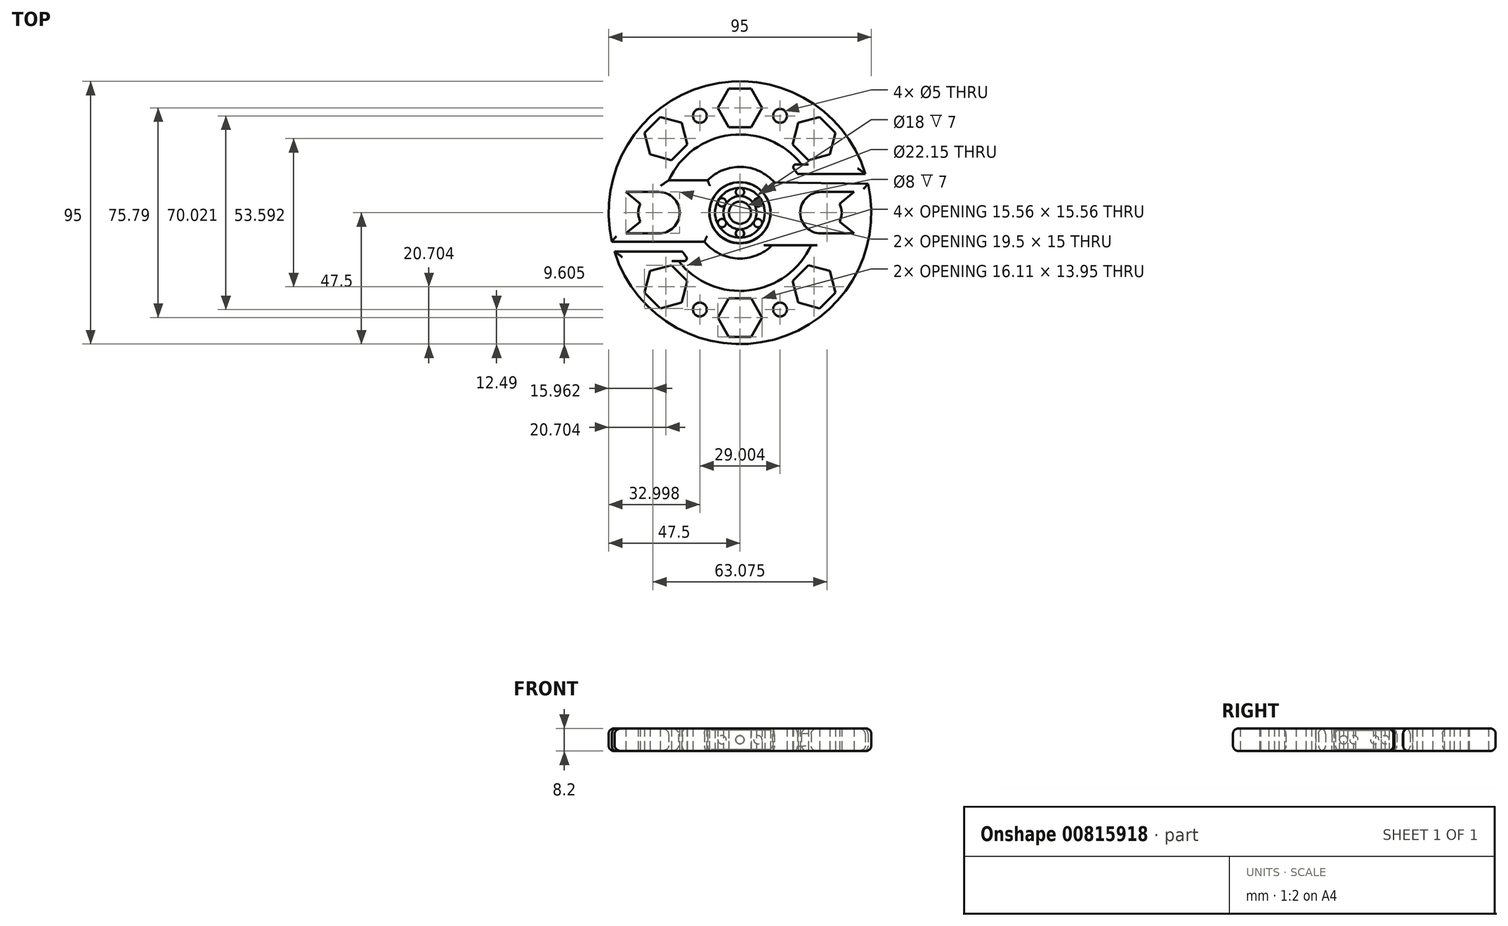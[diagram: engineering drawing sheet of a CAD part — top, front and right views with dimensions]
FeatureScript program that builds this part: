
annotation { "Feature Type Name" : "Feature", "Feature Type Description" : "" }
export const myFeature = defineFeature(function(context is Context, id is Id, definition is map)
    precondition{}
    {
        {
            var Q0;
            Q0=qCreatedBy(makeId("Top.planeOp"),FACE);
            var sketch = newSketch(context, id + "F0", { "sketchPlane" : qUnion([Q0])});
            skArc(sketch, "E0", {"start": v(45.38, 14.04) * mm, "mid": v(-10.46, 46.33) * mm, "end": v(-47, -6.81) * mm});
            skLineSegment(sketch, "E1.top", {"start": v(-45.38, -14.04) * mm, "end": v(-24.56, -14.04) * mm});
            skCircle(sketch, "E2", {"center": v(0, 0) * mm, "radius": 11.07 * mm});
            skArc(sketch, "E3", {"start": v(22.24, 17.5) * mm, "mid": v(-3.38, 28.09) * mm, "end": v(-25.75, 11.72) * mm});
            skArc(sketch, "E4.trimOffspring", {"start": v(-22.2, -17.54) * mm, "mid": v(3.4, -28.08) * mm, "end": v(25.75, -11.72) * mm});
            skArc(sketch, "E5.trimOffspring", {"start": v(-45.38, -14.04) * mm, "mid": v(10.5, -46.32) * mm, "end": v(47, 6.9) * mm});
            skLineSegment(sketch, "E6.trimOffspring", {"start": v(24.59, 14) * mm, "end": v(45.38, 14.04) * mm});
            skPoint(sketch, "E7.trimOffspring.end.orphan", {"position": v(45.38, -14.04) * mm});
            skPoint(sketch, "E1.bottom.start.orphan", {"position": v(-45.38, 14.04) * mm});
            skPoint(sketch, "E8.orphan", {"position": v(47, -6.9) * mm});
            skPoint(sketch, "E9.orphan", {"position": v(-47, 6.81) * mm});
            skArc(sketch, "E10", {"start": v(-12.86, -10.46) * mm, "mid": v(-0.85, -16.55) * mm, "end": v(11.72, -11.72) * mm});
            skArc(sketch, "E11.trimOffspring", {"start": v(12.47, 10.92) * mm, "mid": v(0.55, 16.57) * mm, "end": v(-11.72, 11.72) * mm});
            skLineSegment(sketch, "E12.trimOffspring", {"start": v(-8.7, 6.85) * mm, "end": v(8.59, 7) * mm});
            skLineSegment(sketch, "E13.trimOffspring", {"start": v(-8.7, -6.85) * mm, "end": v(8.69, -6.87) * mm});
            skLineSegment(sketch, "E14", {"start": v(-7.83, 7.83) * mm, "end": v(-6.87, 6.87) * mm});
            skLineSegment(sketch, "E15", {"start": v(6.87, -6.87) * mm, "end": v(7.83, -7.83) * mm});
            skLineSegment(sketch, "E16", {"start": v(-11.72, 11.72) * mm, "end": v(-25.75, 11.72) * mm});
            skLineSegment(sketch, "E17", {"start": v(11.72, -11.72) * mm, "end": v(11.72, -11.72) * mm});
            skArc(sketch, "E18", {"start": v(20.88, 14) * mm, "mid": v(19.54, 15.8) * mm, "end": v(18.05, 17.5) * mm});
            skLineSegment(sketch, "E19", {"start": v(-24.56, -14.04) * mm, "end": v(-20.85, -14.04) * mm});
            skLineSegment(sketch, "E20", {"start": v(24.59, 14) * mm, "end": v(20.88, 14) * mm});
            skLineSegment(sketch, "E21", {"start": v(22.24, 17.5) * mm, "end": v(18.05, 17.5) * mm});
            skLineSegment(sketch, "E22", {"start": v(-22.2, -17.54) * mm, "end": v(-18, -17.54) * mm});
            skArc(sketch, "E23.trimOffspring", {"start": v(-20.85, -14.04) * mm, "mid": v(-19.5, -15.85) * mm, "end": v(-18, -17.54) * mm});
            skLineSegment(sketch, "E24", {"start": v(0, 0) * mm, "end": v(0, 16.57) * mm, "construction": true});
            skLineSegment(sketch, "E25", {"start": v(-6.87, 6.87) * mm, "end": v(-11.72, 11.72) * mm, "construction": true});
            skLineSegment(sketch, "E26", {"start": v(0, 0) * mm, "end": v(11.72, 11.72) * mm, "construction": true});
            skLineSegment(sketch, "E27", {"start": v(6.87, -6.87) * mm, "end": v(11.72, -11.72) * mm, "construction": true});
            skLineSegment(sketch, "E28", {"start": v(0, 0) * mm, "end": v(0, -16.57) * mm, "construction": true});
            skLineSegment(sketch, "E29", {"start": v(0, 0) * mm, "end": v(-11.72, -11.72) * mm, "construction": true});
            skLineSegment(sketch, "E30.trimOffspring", {"start": v(-20, 20) * mm, "end": v(-33.59, 33.59) * mm, "construction": true});
            skLineSegment(sketch, "E31.trimOffspring", {"start": v(0, 28.29) * mm, "end": v(0, 47.5) * mm, "construction": true});
            skLineSegment(sketch, "E32.trimOffspring", {"start": v(20, 20) * mm, "end": v(33.59, 33.59) * mm, "construction": true});
            skLineSegment(sketch, "E33.trimOffspring", {"start": v(20, -20) * mm, "end": v(33.59, -33.59) * mm, "construction": true});
            skLineSegment(sketch, "E34.trimOffspring", {"start": v(0, -28.29) * mm, "end": v(0, -47.5) * mm, "construction": true});
            skLineSegment(sketch, "E35.trimOffspring", {"start": v(-20, -20) * mm, "end": v(-33.59, -33.59) * mm, "construction": true});
            skPoint(sketch, "E36", {"position": v(0, 37.9) * mm});
            skPoint(sketch, "E37", {"position": v(-26.8, 26.8) * mm});
            skPoint(sketch, "E38", {"position": v(26.8, 26.8) * mm});
            skPoint(sketch, "E39", {"position": v(26.8, -26.8) * mm});
            skPoint(sketch, "E40", {"position": v(0, -37.9) * mm});
            skPoint(sketch, "E41", {"position": v(-26.8, -26.8) * mm});
            skLineSegment(sketch, "E42.0", {"start": v(-32.5, 21.1) * mm, "end": v(-34.58, 28.88) * mm});
            skLineSegment(sketch, "E42.1", {"start": v(-34.58, 28.88) * mm, "end": v(-28.88, 34.58) * mm});
            skLineSegment(sketch, "E42.2", {"start": v(-28.88, 34.58) * mm, "end": v(-21.1, 32.5) * mm});
            skLineSegment(sketch, "E42.3", {"start": v(-21.1, 32.5) * mm, "end": v(-19.02, 24.71) * mm});
            skLineSegment(sketch, "E42.4", {"start": v(-19.02, 24.71) * mm, "end": v(-24.71, 19.02) * mm});
            skLineSegment(sketch, "E42.5", {"start": v(-24.71, 19.02) * mm, "end": v(-32.5, 21.1) * mm});
            skLineSegment(sketch, "E43.0", {"start": v(21.1, -32.5) * mm, "end": v(19.02, -24.71) * mm});
            skLineSegment(sketch, "E43.1", {"start": v(19.02, -24.71) * mm, "end": v(24.71, -19.02) * mm});
            skLineSegment(sketch, "E43.2", {"start": v(24.71, -19.02) * mm, "end": v(32.5, -21.1) * mm});
            skLineSegment(sketch, "E43.3", {"start": v(32.5, -21.1) * mm, "end": v(34.58, -28.88) * mm});
            skLineSegment(sketch, "E43.4", {"start": v(34.58, -28.88) * mm, "end": v(28.88, -34.58) * mm});
            skLineSegment(sketch, "E43.5", {"start": v(28.88, -34.58) * mm, "end": v(21.1, -32.5) * mm});
            skLineSegment(sketch, "E44.0", {"start": v(-8.05, 37.9) * mm, "end": v(-4.03, 44.87) * mm});
            skLineSegment(sketch, "E44.1", {"start": v(-4.03, 44.87) * mm, "end": v(4.03, 44.87) * mm});
            skLineSegment(sketch, "E44.2", {"start": v(4.03, 44.87) * mm, "end": v(8.05, 37.9) * mm});
            skLineSegment(sketch, "E44.3", {"start": v(8.05, 37.9) * mm, "end": v(4.03, 30.92) * mm});
            skLineSegment(sketch, "E44.4", {"start": v(4.03, 30.92) * mm, "end": v(-4.03, 30.92) * mm});
            skLineSegment(sketch, "E44.5", {"start": v(-4.03, 30.92) * mm, "end": v(-8.05, 37.9) * mm});
            skLineSegment(sketch, "E45.0", {"start": v(-8.05, -37.9) * mm, "end": v(-4.03, -30.92) * mm});
            skLineSegment(sketch, "E45.1", {"start": v(-4.03, -30.92) * mm, "end": v(4.03, -30.92) * mm});
            skLineSegment(sketch, "E45.2", {"start": v(4.03, -30.92) * mm, "end": v(8.05, -37.9) * mm});
            skLineSegment(sketch, "E45.3", {"start": v(8.05, -37.9) * mm, "end": v(4.03, -44.87) * mm});
            skLineSegment(sketch, "E45.4", {"start": v(4.03, -44.87) * mm, "end": v(-4.03, -44.87) * mm});
            skLineSegment(sketch, "E45.5", {"start": v(-4.03, -44.87) * mm, "end": v(-8.05, -37.9) * mm});
            skLineSegment(sketch, "E46.0", {"start": v(-32.5, -21.1) * mm, "end": v(-24.71, -19.02) * mm});
            skLineSegment(sketch, "E46.1", {"start": v(-24.71, -19.02) * mm, "end": v(-19.02, -24.71) * mm});
            skLineSegment(sketch, "E46.2", {"start": v(-19.02, -24.71) * mm, "end": v(-21.1, -32.5) * mm});
            skLineSegment(sketch, "E46.3", {"start": v(-21.1, -32.5) * mm, "end": v(-28.88, -34.58) * mm});
            skLineSegment(sketch, "E46.4", {"start": v(-28.88, -34.58) * mm, "end": v(-34.58, -28.88) * mm});
            skLineSegment(sketch, "E46.5", {"start": v(-34.58, -28.88) * mm, "end": v(-32.5, -21.1) * mm});
            skLineSegment(sketch, "E47.0", {"start": v(21.1, 32.5) * mm, "end": v(28.88, 34.58) * mm});
            skLineSegment(sketch, "E47.1", {"start": v(28.88, 34.58) * mm, "end": v(34.58, 28.88) * mm});
            skLineSegment(sketch, "E47.2", {"start": v(34.58, 28.88) * mm, "end": v(32.5, 21.1) * mm});
            skLineSegment(sketch, "E47.3", {"start": v(32.5, 21.1) * mm, "end": v(24.71, 19.02) * mm});
            skLineSegment(sketch, "E47.4", {"start": v(24.71, 19.02) * mm, "end": v(19.02, 24.71) * mm});
            skLineSegment(sketch, "E47.5", {"start": v(19.02, 24.71) * mm, "end": v(21.1, 32.5) * mm});
            skArc(sketch, "E48", {"start": v(-45.38, -14.04) * mm, "mid": v(10.5, -46.32) * mm, "end": v(47, 6.9) * mm, "construction": true});
            skArc(sketch, "E49", {"start": v(-47, -6.81) * mm, "mid": v(-46.7, -8.64) * mm, "end": v(-46.33, -10.46) * mm});
            skPoint(sketch, "E50", {"position": v(-46.33, -10.46) * mm});
            skArc(sketch, "E51", {"start": v(45.38, 14.04) * mm, "mid": v(-10.46, 46.33) * mm, "end": v(-47, -6.81) * mm, "construction": true});
            skArc(sketch, "E52", {"start": v(47, 6.9) * mm, "mid": v(46.7, 8.71) * mm, "end": v(46.32, 10.5) * mm});
            skPoint(sketch, "E53", {"position": v(46.32, 10.5) * mm});
            skLineSegment(sketch, "E54", {"start": v(-46.33, -10.46) * mm, "end": v(-36.42, -10.46) * mm});
            skLineSegment(sketch, "E55", {"start": v(46.32, 10.5) * mm, "end": v(12.47, 10.92) * mm});
            skPoint(sketch, "E56", {"position": v(-114.88, 3.23) * mm});
            skLineSegment(sketch, "E57.0", {"start": v(-114.88, 9.7) * mm, "end": v(-109.28, 6.47) * mm});
            skLineSegment(sketch, "E57.1", {"start": v(-109.28, 6.47) * mm, "end": v(-109.28, 0) * mm});
            skLineSegment(sketch, "E57.2", {"start": v(-109.28, 0) * mm, "end": v(-114.88, -3.23) * mm});
            skLineSegment(sketch, "E57.3", {"start": v(-114.88, -3.23) * mm, "end": v(-120.48, 0) * mm});
            skLineSegment(sketch, "E57.4", {"start": v(-120.48, 0) * mm, "end": v(-120.48, 6.47) * mm});
            skLineSegment(sketch, "E57.5", {"start": v(-120.48, 6.47) * mm, "end": v(-114.88, 9.7) * mm});
            skPoint(sketch, "E58", {"position": v(-130.27, -23) * mm});
            skLineSegment(sketch, "E59.0", {"start": v(-130.27, -16.53) * mm, "end": v(-124.67, -19.77) * mm});
            skLineSegment(sketch, "E59.1", {"start": v(-124.67, -19.77) * mm, "end": v(-124.67, -26.23) * mm});
            skLineSegment(sketch, "E59.2", {"start": v(-124.67, -26.23) * mm, "end": v(-130.27, -29.47) * mm});
            skLineSegment(sketch, "E59.3", {"start": v(-130.27, -29.47) * mm, "end": v(-135.87, -26.23) * mm});
            skLineSegment(sketch, "E59.4", {"start": v(-135.87, -26.23) * mm, "end": v(-135.87, -19.77) * mm});
            skLineSegment(sketch, "E59.5", {"start": v(-135.87, -19.77) * mm, "end": v(-130.27, -16.53) * mm});
            skLineSegment(sketch, "E60", {"start": v(-11.07, 0) * mm, "end": v(-47.5, 0) * mm, "construction": true});
            skLineSegment(sketch, "E61", {"start": v(11.07, 0) * mm, "end": v(47.5, 0) * mm, "construction": true});
            skLineSegment(sketch, "E62.0", {"start": v(-137.37, -18.9) * mm, "end": v(-130.27, -14.8) * mm});
            skLineSegment(sketch, "E62.1", {"start": v(-123.17, -18.9) * mm, "end": v(-123.17, -27.1) * mm});
            skLineSegment(sketch, "E62.2", {"start": v(-123.17, -27.1) * mm, "end": v(-130.27, -31.2) * mm});
            skLineSegment(sketch, "E62.3", {"start": v(-130.27, -14.8) * mm, "end": v(-123.17, -18.9) * mm});
            skLineSegment(sketch, "E62.4", {"start": v(-130.27, -31.2) * mm, "end": v(-137.37, -27.1) * mm});
            skLineSegment(sketch, "E62.5", {"start": v(-137.37, -27.1) * mm, "end": v(-137.37, -18.9) * mm});
            skLineSegment(sketch, "E63.0", {"start": v(-138.87, -18.03) * mm, "end": v(-130.27, -13.07) * mm});
            skLineSegment(sketch, "E63.1", {"start": v(-121.67, -18.03) * mm, "end": v(-121.67, -27.97) * mm});
            skLineSegment(sketch, "E63.2", {"start": v(-121.67, -27.97) * mm, "end": v(-130.27, -32.93) * mm});
            skLineSegment(sketch, "E63.3", {"start": v(-130.27, -13.07) * mm, "end": v(-121.67, -18.03) * mm});
            skLineSegment(sketch, "E63.4", {"start": v(-130.27, -32.93) * mm, "end": v(-138.87, -27.97) * mm});
            skLineSegment(sketch, "E63.5", {"start": v(-138.87, -27.97) * mm, "end": v(-138.87, -18.03) * mm});
            skPoint(sketch, "E64", {"position": v(-99.9, -24.26) * mm});
            skLineSegment(sketch, "E65.0", {"start": v(-109.83, -24.26) * mm, "end": v(-104.87, -15.66) * mm});
            skLineSegment(sketch, "E65.1", {"start": v(-94.94, -15.66) * mm, "end": v(-89.97, -24.26) * mm});
            skLineSegment(sketch, "E65.2", {"start": v(-89.97, -24.26) * mm, "end": v(-94.94, -32.86) * mm});
            skLineSegment(sketch, "E65.3", {"start": v(-104.87, -15.66) * mm, "end": v(-94.94, -15.66) * mm});
            skLineSegment(sketch, "E65.4", {"start": v(-94.94, -32.86) * mm, "end": v(-104.87, -32.86) * mm});
            skLineSegment(sketch, "E65.5", {"start": v(-104.87, -32.86) * mm, "end": v(-109.83, -24.26) * mm});
            skLineSegment(sketch, "E66.0", {"start": v(-107.82, -22.14) * mm, "end": v(-102.03, -16.34) * mm});
            skLineSegment(sketch, "E66.1", {"start": v(-94.1, -18.47) * mm, "end": v(-91.98, -26.38) * mm});
            skLineSegment(sketch, "E66.2", {"start": v(-91.98, -26.38) * mm, "end": v(-97.78, -32.18) * mm});
            skLineSegment(sketch, "E66.3", {"start": v(-102.03, -16.34) * mm, "end": v(-94.1, -18.47) * mm});
            skLineSegment(sketch, "E66.4", {"start": v(-97.78, -32.18) * mm, "end": v(-105.7, -30.06) * mm});
            skLineSegment(sketch, "E66.5", {"start": v(-105.7, -30.06) * mm, "end": v(-107.82, -22.14) * mm});
            skLineSegment(sketch, "E67.0", {"start": v(-99.9, -17.8) * mm, "end": v(-94.3, -21.03) * mm});
            skLineSegment(sketch, "E67.1", {"start": v(-94.3, -21.03) * mm, "end": v(-94.3, -27.5) * mm});
            skLineSegment(sketch, "E67.2", {"start": v(-94.3, -27.5) * mm, "end": v(-99.9, -30.73) * mm});
            skLineSegment(sketch, "E67.3", {"start": v(-99.9, -30.73) * mm, "end": v(-105.5, -27.5) * mm});
            skLineSegment(sketch, "E67.4", {"start": v(-105.5, -27.5) * mm, "end": v(-105.5, -21.03) * mm});
            skLineSegment(sketch, "E67.5", {"start": v(-105.5, -21.03) * mm, "end": v(-99.9, -17.8) * mm});
            skLineSegment(sketch, "E68.0", {"start": v(-111.57, -24.26) * mm, "end": v(-105.73, -14.16) * mm});
            skLineSegment(sketch, "E68.1", {"start": v(-94.07, -14.16) * mm, "end": v(-88.24, -24.26) * mm});
            skLineSegment(sketch, "E68.2", {"start": v(-88.24, -24.26) * mm, "end": v(-94.07, -34.36) * mm});
            skLineSegment(sketch, "E68.3", {"start": v(-105.73, -14.16) * mm, "end": v(-94.07, -14.16) * mm});
            skLineSegment(sketch, "E68.4", {"start": v(-94.07, -34.36) * mm, "end": v(-105.73, -34.36) * mm});
            skLineSegment(sketch, "E68.5", {"start": v(-105.73, -34.36) * mm, "end": v(-111.57, -24.26) * mm});
            skArc(sketch, "E69", {"start": v(-12.86, -10.46) * mm, "mid": v(16.55, -0.85) * mm, "end": v(-11.72, 11.72) * mm, "construction": true});
            skArc(sketch, "E70", {"start": v(-11.72, 11.72) * mm, "mid": v(-16.55, 0.85) * mm, "end": v(-12.86, -10.46) * mm, "construction": true});
            skLineSegment(sketch, "E71", {"start": v(11.72, -11.72) * mm, "end": v(25.75, -11.72) * mm});
            skLineSegment(sketch, "E72", {"start": v(12.47, 10.92) * mm, "end": v(12.47, 10.92) * mm});
            skArc(sketch, "E73", {"start": v(-20.87, 31.63) * mm, "mid": v(-26.8, 26.8) * mm, "end": v(-31.63, 20.87) * mm, "construction": true});
            skArc(sketch, "E74", {"start": v(-7.6, 37.12) * mm, "mid": v(-14.5, 35.01) * mm, "end": v(-20.87, 31.63) * mm, "construction": true});
            skArc(sketch, "E75", {"start": v(7.6, 37.12) * mm, "mid": v(0, 37.9) * mm, "end": v(-7.6, 37.12) * mm, "construction": true});
            skArc(sketch, "E76", {"start": v(20.87, 31.63) * mm, "mid": v(14.5, 35.01) * mm, "end": v(7.6, 37.12) * mm, "construction": true});
            skCircle(sketch, "E77", {"center": v(-14.5, 35.01) * mm, "radius": 2.5 * mm});
            skCircle(sketch, "E78", {"center": v(14.5, 35.01) * mm, "radius": 2.5 * mm});
            skCircle(sketch, "E79.MirrorC", {"center": v(-14.5, -35.01) * mm, "radius": 2.5 * mm});
            skCircle(sketch, "E80.MirrorC", {"center": v(14.5, -35.01) * mm, "radius": 2.5 * mm});
            skLineSegment(sketch, "E81", {"start": v(-31.63, 20.87) * mm, "end": v(-31.63, 20.87) * mm});
            skLineSegment(sketch, "E82", {"start": v(-36.42, -10.46) * mm, "end": v(-12.86, -10.46) * mm});
            skPoint(sketch, "E83", {"position": v(-31.63, 20.87) * mm});
            skPoint(sketch, "E84", {"position": v(-36.42, -10.46) * mm});
            skArc(sketch, "E85", {"start": v(-31.63, 20.87) * mm, "mid": v(-37.46, 5.73) * mm, "end": v(-36.42, -10.46) * mm, "construction": true});
            skArc(sketch, "E86", {"start": v(-36.42, -10.46) * mm, "mid": v(22.43, -30.54) * mm, "end": v(20.87, 31.63) * mm, "construction": true});
            skPoint(sketch, "E87", {"position": v(-37.04, -8) * mm});
            skCircle(sketch, "E88", {"center": v(-72.26, 0) * mm, "radius": 7.5 * mm});
            skLineSegment(sketch, "E89", {"start": v(-72.26, 7.5) * mm, "end": v(-84.26, 7.5) * mm});
            skLineSegment(sketch, "E90", {"start": v(-84.26, 7.5) * mm, "end": v(-79.03, 3.23) * mm});
            skLineSegment(sketch, "E91.MirrorCS", {"start": v(-72.26, 11.35) * mm, "end": v(-72.26, 11.35) * mm});
            skLineSegment(sketch, "E92.MirrorCS", {"start": v(-84.26, -7.5) * mm, "end": v(-79.03, -3.23) * mm});
            skPoint(sketch, "E93", {"position": v(-72.26, 11.35) * mm});
            skLineSegment(sketch, "E94", {"start": v(-84.26, -7.5) * mm, "end": v(-72.26, -7.5) * mm});
            skCircle(sketch, "E95", {"center": v(-29.29, 0) * mm, "radius": 7.5 * mm});
            skLineSegment(sketch, "E96", {"start": v(-29.29, 7.5) * mm, "end": v(-41.29, 7.5) * mm});
            skLineSegment(sketch, "E97", {"start": v(-41.29, 7.5) * mm, "end": v(-36.06, 3.23) * mm});
            skLineSegment(sketch, "E98.MirrorCS", {"start": v(-58.17, -2.6) * mm, "end": v(-58.17, -2.6) * mm});
            skLineSegment(sketch, "E99.MirrorCS", {"start": v(-41.29, -7.5) * mm, "end": v(-36.06, -3.23) * mm});
            skPoint(sketch, "E100", {"position": v(-29.29, 11.35) * mm});
            skLineSegment(sketch, "E101", {"start": v(-41.29, -7.5) * mm, "end": v(-29.29, -7.5) * mm});
            skCircle(sketch, "E102", {"center": v(29.29, 0) * mm, "radius": 7.5 * mm});
            skLineSegment(sketch, "E103", {"start": v(29.29, -7.5) * mm, "end": v(41.29, -7.5) * mm});
            skLineSegment(sketch, "E104", {"start": v(41.29, -7.5) * mm, "end": v(36.06, -3.23) * mm});
            skLineSegment(sketch, "E105.MirrorCS", {"start": v(-45.35, -43.19) * mm, "end": v(-45.35, -43.19) * mm});
            skLineSegment(sketch, "E106.MirrorCS", {"start": v(41.29, 7.5) * mm, "end": v(36.06, 3.23) * mm});
            skPoint(sketch, "E107", {"position": v(29.29, -11.35) * mm});
            skLineSegment(sketch, "E108", {"start": v(41.29, 7.5) * mm, "end": v(29.29, 7.5) * mm});
            skSolve(sketch);
        }
        {
            var Q0;
            Q0=makeQuery(id+"F0.imprint","IMPRINT",FACE,{"disambiguationData":[TD([[makeQuery(id+"F0.imprint","IMPRINT",EDGE,{"derivedFrom":sQuery(id+"F0.wireOp",EDGE,"E0")}),1.0]])]});
            extrude(context, id + "F1", {"entities" : qUnion([Q0]), "endBound" : BoundingType.SYMMETRIC, "depth" : 8.2 * mm, "offsetDistance" : 25 * mm});
        }
        {
            var Q0;
            Q0=makeQuery(id+"F1.opExtrude","CAP_EDGE",EDGE,{"disambiguationData":[OSD([sQuery(id+"F0.wireOp",EDGE,"E0")])],"isStart":false});
            var Q1;
            Q1=makeQuery(id+"F1.opExtrude","CAP_EDGE",EDGE,{"disambiguationData":[OSD([sQuery(id+"F0.wireOp",EDGE,"E5.trimOffspring")])],"isStart":false});
            var Q2;
            Q2=makeQuery(id+"F1.opExtrude","CAP_EDGE",EDGE,{"disambiguationData":[OSD([sQuery(id+"F0.wireOp",EDGE,"E0")])],"isStart":true});
            var Q3;
            Q3=makeQuery(id+"F1.opExtrude","CAP_EDGE",EDGE,{"disambiguationData":[OSD([sQuery(id+"F0.wireOp",EDGE,"E5.trimOffspring")])],"isStart":true});
            var Q4;
            Q4=makeQuery(id+"F1.opExtrude","CAP_EDGE",EDGE,{"disambiguationData":[OSD([sQuery(id+"F0.wireOp",EDGE,"E1.top"),sQuery(id+"F0.wireOp",EDGE,"E19")])],"isStart":true});
            var Q5;
            Q5=makeQuery(id+"F1.opExtrude","CAP_EDGE",EDGE,{"disambiguationData":[OSD([sQuery(id+"F0.wireOp",EDGE,"E1.top"),sQuery(id+"F0.wireOp",EDGE,"E19")])],"isStart":false});
            var Q6;
            Q6=makeQuery(id+"F1.opExtrude","CAP_EDGE",EDGE,{"disambiguationData":[OSD([sQuery(id+"F0.wireOp",EDGE,"af73f036-c247-4c71-b03d-1512b0a657ec.trimOffspring")])],"isStart":true});
            var Q7;
            Q7=makeQuery(id+"F1.opExtrude","CAP_EDGE",EDGE,{"disambiguationData":[OSD([sQuery(id+"F0.wireOp",EDGE,"af73f036-c247-4c71-b03d-1512b0a657ec.trimOffspring")])],"isStart":false});
            var Q8;
            Q8=makeQuery(id+"F1.opExtrude","CAP_EDGE",EDGE,{"disambiguationData":[OSD([sQuery(id+"F0.wireOp",EDGE,"E11.trimOffspring")])],"isStart":false});
            var Q9;
            Q9=makeQuery(id+"F1.opExtrude","CAP_EDGE",EDGE,{"disambiguationData":[OSD([sQuery(id+"F0.wireOp",EDGE,"E11.trimOffspring")])],"isStart":true});
            var Q10;
            Q10=makeQuery(id+"F1.opExtrude","CAP_EDGE",EDGE,{"disambiguationData":[OSD([sQuery(id+"F0.wireOp",EDGE,"E16")])],"isStart":false});
            var Q11;
            Q11=makeQuery(id+"F1.opExtrude","CAP_EDGE",EDGE,{"disambiguationData":[OSD([sQuery(id+"F0.wireOp",EDGE,"E16")])],"isStart":true});
            var Q12;
            Q12=makeQuery(id+"F1.opExtrude","CAP_EDGE",EDGE,{"disambiguationData":[OSD([sQuery(id+"F0.wireOp",EDGE,"E4.trimOffspring")])],"isStart":true});
            var Q13;
            Q13=makeQuery(id+"F1.opExtrude","CAP_EDGE",EDGE,{"disambiguationData":[OSD([sQuery(id+"F0.wireOp",EDGE,"E4.trimOffspring")])],"isStart":false});
            var Q14;
            Q14=makeQuery(id+"F1.opExtrude","CAP_EDGE",EDGE,{"disambiguationData":[OSD([sQuery(id+"F0.wireOp",EDGE,"E3")])],"isStart":false});
            var Q15;
            Q15=makeQuery(id+"F1.opExtrude","CAP_EDGE",EDGE,{"disambiguationData":[OSD([sQuery(id+"F0.wireOp",EDGE,"E3")])],"isStart":true});
            var Q16;
            Q16=makeQuery(id+"F1.opExtrude","CAP_EDGE",EDGE,{"disambiguationData":[OSD([sQuery(id+"F0.wireOp",EDGE,"E17")])],"isStart":false});
            var Q17;
            Q17=makeQuery(id+"F1.opExtrude","CAP_EDGE",EDGE,{"disambiguationData":[OSD([sQuery(id+"F0.wireOp",EDGE,"E17")])],"isStart":true});
            var Q18;
            Q18=makeQuery(id+"F1.opExtrude","CAP_EDGE",EDGE,{"disambiguationData":[OSD([sQuery(id+"F0.wireOp",EDGE,"E10")])],"isStart":false});
            var Q19;
            Q19=makeQuery(id+"F1.opExtrude","CAP_EDGE",EDGE,{"disambiguationData":[OSD([sQuery(id+"F0.wireOp",EDGE,"E10")])],"isStart":true});
            var Q20;
            Q20=makeQuery(id+"F1.opExtrude","CAP_EDGE",EDGE,{"disambiguationData":[OSD([sQuery(id+"F0.wireOp",EDGE,"318f1a37-417c-41ab-8845-f020125537680.MirrorCS")])],"isStart":false});
            var Q21;
            Q21=makeQuery(id+"F1.opExtrude","CAP_EDGE",EDGE,{"disambiguationData":[OSD([sQuery(id+"F0.wireOp",EDGE,"318f1a37-417c-41ab-8845-f020125537680.MirrorCS")])],"isStart":true});
            var Q22;
            Q22=makeQuery(id+"F1.opExtrude","CAP_EDGE",EDGE,{"disambiguationData":[OSD([sQuery(id+"F0.wireOp",EDGE,"E6.trimOffspring")])],"isStart":false});
            var Q23;
            Q23=makeQuery(id+"F1.opExtrude","CAP_EDGE",EDGE,{"disambiguationData":[OSD([sQuery(id+"F0.wireOp",EDGE,"E6.trimOffspring")])],"isStart":true});
            var Q24;
            Q24=makeQuery(id+"F1.opExtrude","CAP_EDGE",EDGE,{"disambiguationData":[OSD([sQuery(id+"F0.wireOp",EDGE,"E54")])],"isStart":false});
            var Q25;
            Q25=makeQuery(id+"F1.opExtrude","CAP_EDGE",EDGE,{"disambiguationData":[OSD([sQuery(id+"F0.wireOp",EDGE,"E54")])],"isStart":true});
            var Q26;
            Q26=makeQuery(id+"F1.opExtrude","CAP_EDGE",EDGE,{"disambiguationData":[OSD([sQuery(id+"F0.wireOp",EDGE,"E55")])],"isStart":true});
            var Q27;
            Q27=makeQuery(id+"F1.opExtrude","CAP_EDGE",EDGE,{"disambiguationData":[OSD([sQuery(id+"F0.wireOp",EDGE,"E55")])],"isStart":false});
            fillet(context, id + "F2", {"entities" : qUnion([Q0, Q1, Q2, Q3, Q4, Q5, Q6, Q7, Q8, Q9, Q10, Q11, Q12, Q13, Q14, Q15, Q16, Q17, Q18, Q19, Q20, Q21, Q22, Q23, Q24, Q25, Q26, Q27]), "radius" : 2 * mm, "tangentPropagation" : true, "allowEdgeOverflow" : false});
        }
        {
            var Q0;
            Q0=qCreatedBy(makeId("Top.planeOp"),FACE);
            var sketch = newSketch(context, id + "F3", { "sketchPlane" : qUnion([Q0])});
            skCircle(sketch, "E109", {"center": v(56.9, -63.65) * mm, "radius": 11 * mm});
            skCircle(sketch, "E110", {"center": v(56.9, -63.65) * mm, "radius": 9 * mm});
            skCircle(sketch, "E111", {"center": v(56.9, -63.65) * mm, "radius": 4 * mm});
            skCircle(sketch, "E112", {"center": v(56.9, -63.65) * mm, "radius": 6 * mm});
            skArc(sketch, "E113", {"start": v(56.9, -57.65) * mm, "mid": v(58.4, -56.15) * mm, "end": v(56.9, -54.65) * mm});
            skArc(sketch, "E114.1.0", {"start": v(63.4, -61.4) * mm, "mid": v(64.9, -59.9) * mm, "end": v(63.4, -58.4) * mm});
            skArc(sketch, "E114.2.0", {"start": v(63.4, -68.9) * mm, "mid": v(64.9, -67.4) * mm, "end": v(63.4, -65.9) * mm});
            skArc(sketch, "E114.3.0", {"start": v(56.9, -72.65) * mm, "mid": v(58.4, -71.14) * mm, "end": v(56.88, -69.65) * mm});
            skArc(sketch, "E114.4.0", {"start": v(50.41, -68.9) * mm, "mid": v(51.91, -67.4) * mm, "end": v(50.41, -65.9) * mm});
            skArc(sketch, "E114.5.0", {"start": v(50.41, -61.4) * mm, "mid": v(51.91, -59.9) * mm, "end": v(50.41, -58.4) * mm});
            skLineSegment(sketch, "E115", {"start": v(50.41, -65.9) * mm, "end": v(50.41, -68.9) * mm});
            skLineSegment(sketch, "E116", {"start": v(56.88, -69.65) * mm, "end": v(56.9, -72.65) * mm});
            skLineSegment(sketch, "E117", {"start": v(63.4, -65.9) * mm, "end": v(63.4, -68.9) * mm});
            skLineSegment(sketch, "E118", {"start": v(63.4, -58.4) * mm, "end": v(63.4, -61.4) * mm});
            skLineSegment(sketch, "E119", {"start": v(56.9, -54.65) * mm, "end": v(56.9, -54.65) * mm});
            skLineSegment(sketch, "E120", {"start": v(50.41, -58.4) * mm, "end": v(50.41, -61.4) * mm});
            skLineSegment(sketch, "E121.trimOffspring", {"start": v(56.9, -57.65) * mm, "end": v(56.9, -57.65) * mm});
            skLineSegment(sketch, "E122.trimOffspring", {"start": v(51.71, -60.65) * mm, "end": v(51.71, -60.65) * mm});
            skLineSegment(sketch, "E123", {"start": v(56.9, -57.65) * mm, "end": v(56.9, -54.65) * mm});
            skSolve(sketch);
        }
        {
            var Q0;
            Q0=makeQuery(id+"F3.imprint","IMPRINT",FACE,{"disambiguationData":[TD([[makeQuery(id+"F3.imprint","IMPRINT",EDGE,{"derivedFrom":sQuery(id+"F3.wireOp",EDGE,"E109")}),1.0]])]});
            var Q1;
            Q1=makeQuery(id+"F3.imprint","IMPRINT",FACE,{"disambiguationData":[TD([[makeQuery(id+"F3.imprint","IMPRINT",EDGE,{"derivedFrom":sQuery(id+"F3.wireOp",EDGE,"E111")}),-1.0]])]});
            extrude(context, id + "F4", {"entities" : qUnion([Q0, Q1]), "endBound" : BoundingType.SYMMETRIC, "depth" : 7 * mm, "offsetDistance" : 25 * mm});
        }
        {
            var Q0;
            Q0=makeQuery(id+"F3.imprint","IMPRINT",FACE,{"disambiguationData":[TD([[makeQuery(id+"F3.imprint","IMPRINT",EDGE,{"derivedFrom":sQuery(id+"F3.wireOp",EDGE,"E113")}),1.0]])]});
            var Q1;
            Q1=sQuery(id+"F3.wireOp",EDGE,"E123");
            revolve(context, id + "F5", {"surfaceOperationType" : NewSurfaceOperationType.NEW, "entities" : qUnion([Q0]), "axis" : qUnion([Q1]), "revolveType" : RevolveType.FULL});
        }
        {
            var Q0;
            {var subQ0=sQuery(id+"F3.wireOp",EDGE,"E118");Q0=makeQuery(id+"F3.imprint","IMPRINT",FACE,{"disambiguationData":[TD([[makeQuery(id+"F3.imprint","IMPRINT",EDGE,{"derivedFrom":subQ0}),1.0]])]});}
            var Q1;
            Q1=sQuery(id+"F3.wireOp",EDGE,"E118");
            revolve(context, id + "F6", {"surfaceOperationType" : NewSurfaceOperationType.NEW, "entities" : qUnion([Q0]), "axis" : qUnion([Q1]), "revolveType" : RevolveType.FULL});
        }
        {
            var Q0;
            {var subQ0=sQuery(id+"F3.wireOp",EDGE,"E120");Q0=makeQuery(id+"F3.imprint","IMPRINT",FACE,{"disambiguationData":[TD([[makeQuery(id+"F3.imprint","IMPRINT",EDGE,{"derivedFrom":subQ0}),1.0]])]});}
            var Q1;
            Q1=sQuery(id+"F3.wireOp",EDGE,"E120");
            revolve(context, id + "F7", {"surfaceOperationType" : NewSurfaceOperationType.NEW, "entities" : qUnion([Q0]), "axis" : qUnion([Q1]), "revolveType" : RevolveType.FULL});
        }
        {
            var Q0;
            {var subQ0=sQuery(id+"F3.wireOp",EDGE,"E115");Q0=makeQuery(id+"F3.imprint","IMPRINT",FACE,{"disambiguationData":[TD([[makeQuery(id+"F3.imprint","IMPRINT",EDGE,{"derivedFrom":subQ0}),1.0]])]});}
            var Q1;
            Q1=sQuery(id+"F3.wireOp",EDGE,"E115");
            revolve(context, id + "F8", {"surfaceOperationType" : NewSurfaceOperationType.NEW, "entities" : qUnion([Q0]), "axis" : qUnion([Q1]), "revolveType" : RevolveType.FULL});
        }
        {
            var Q0;
            {var subQ0=sQuery(id+"F3.wireOp",EDGE,"E117");Q0=makeQuery(id+"F3.imprint","IMPRINT",FACE,{"disambiguationData":[TD([[makeQuery(id+"F3.imprint","IMPRINT",EDGE,{"derivedFrom":subQ0}),1.0]])]});}
            var Q1;
            Q1=sQuery(id+"F3.wireOp",EDGE,"E117");
            revolve(context, id + "F9", {"surfaceOperationType" : NewSurfaceOperationType.NEW, "entities" : qUnion([Q0]), "axis" : qUnion([Q1]), "revolveType" : RevolveType.FULL});
        }
        {
            var Q0;
            {var subQ0=sQuery(id+"F3.wireOp",EDGE,"E116");Q0=makeQuery(id+"F3.imprint","IMPRINT",FACE,{"disambiguationData":[TD([[makeQuery(id+"F3.imprint","IMPRINT",EDGE,{"derivedFrom":subQ0}),1.0]])]});}
            var Q1;
            Q1=sQuery(id+"F3.wireOp",EDGE,"E116");
            revolve(context, id + "F10", {"surfaceOperationType" : NewSurfaceOperationType.NEW, "entities" : qUnion([Q0]), "axis" : qUnion([Q1]), "revolveType" : RevolveType.FULL});
        }
        {
            var Q0;
            Q0=makeQuery(id+"F6.opRevolve","SWEPT_BODY",BODY,{"disambiguationData":[OSD([sQuery(id+"F3.wireOp",EDGE,"E114.1.0"),sQuery(id+"F3.wireOp",EDGE,"E118")])]});
            var Q1;
            Q1=makeQuery(id+"F5.opRevolve","SWEPT_BODY",BODY,{"disambiguationData":[OSD([sQuery(id+"F3.wireOp",EDGE,"E113"),sQuery(id+"F3.wireOp",EDGE,"E123")])]});
            var Q2;
            Q2=makeQuery(id+"F4.opExtrude","SWEPT_BODY",BODY,{"disambiguationData":[OSD([sQuery(id+"F3.wireOp",EDGE,"E111"),sQuery(id+"F3.wireOp",EDGE,"E112")])]});
            var Q3;
            Q3=makeQuery(id+"F9.opRevolve","SWEPT_BODY",BODY,{"disambiguationData":[OSD([sQuery(id+"F3.wireOp",EDGE,"E114.2.0"),sQuery(id+"F3.wireOp",EDGE,"E117")])]});
            var Q4;
            Q4=makeQuery(id+"F7.opRevolve","SWEPT_BODY",BODY,{"disambiguationData":[OSD([sQuery(id+"F3.wireOp",EDGE,"E114.5.0"),sQuery(id+"F3.wireOp",EDGE,"E120")])]});
            var Q5;
            Q5=makeQuery(id+"F4.opExtrude","SWEPT_BODY",BODY,{"disambiguationData":[OSD([sQuery(id+"F3.wireOp",EDGE,"E109"),sQuery(id+"F3.wireOp",EDGE,"E110")])]});
            var Q6;
            Q6=makeQuery(id+"F10.opRevolve","SWEPT_BODY",BODY,{"disambiguationData":[OSD([sQuery(id+"F3.wireOp",EDGE,"E114.3.0"),sQuery(id+"F3.wireOp",EDGE,"E116")])]});
            var Q7;
            Q7=makeQuery(id+"F8.opRevolve","SWEPT_BODY",BODY,{"disambiguationData":[OSD([sQuery(id+"F3.wireOp",EDGE,"E114.4.0"),sQuery(id+"F3.wireOp",EDGE,"E115")])]});
            transform(context, id + "F11", {"entities" : qUnion([Q0, Q1, Q2, Q3, Q4, Q5, Q6, Q7]), "transformType" : TransformType.TRANSLATION_3D, "dx" : -56.9 * mm, "dy" : 63.65 * mm, "dz" : 0 * mm, "makeCopy" : false});
        }
        {
            var Q0;
            Q0=makeQuery(id+"F1.opExtrude","SWEPT_EDGE",EDGE,{"disambiguationData":[OSD([sQuery(id+"F0.wireOp",EDGE,"E18"),sQuery(id+"F0.wireOp",EDGE,"E21")])]});
            var Q1;
            Q1=makeQuery(id+"F1.opExtrude","SWEPT_EDGE",EDGE,{"disambiguationData":[OSD([sQuery(id+"F0.wireOp",EDGE,"E22"),sQuery(id+"F0.wireOp",EDGE,"E23.trimOffspring")])]});
            fillet(context, id + "F12", {"entities" : qUnion([Q0, Q1]), "radius" : 1 * mm, "tangentPropagation" : true, "allowEdgeOverflow" : false});
        }
    });
